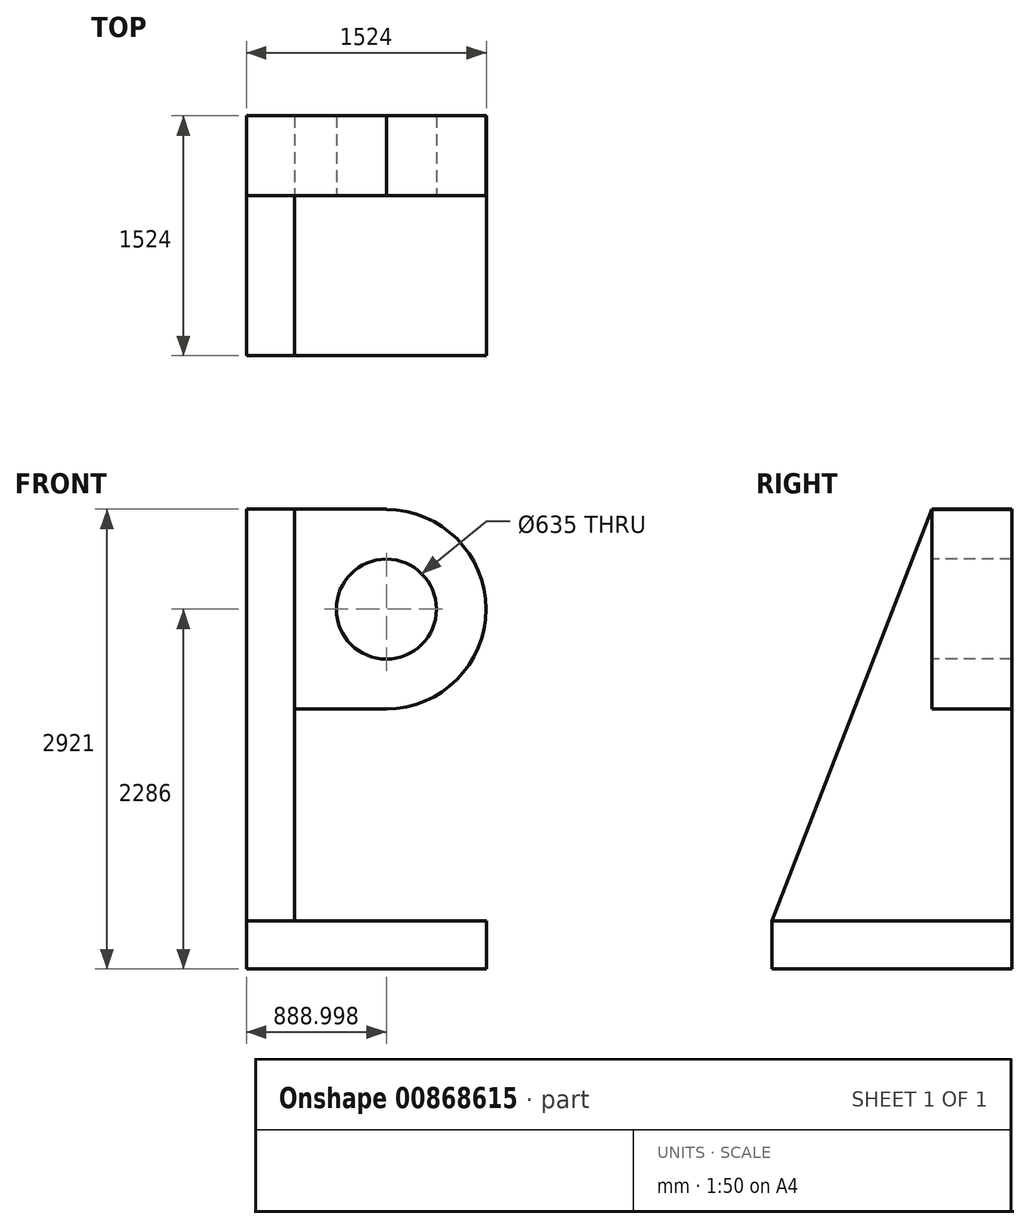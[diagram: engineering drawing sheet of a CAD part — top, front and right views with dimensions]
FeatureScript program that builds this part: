
annotation { "Feature Type Name" : "Feature", "Feature Type Description" : "" }
export const myFeature = defineFeature(function(context is Context, id is Id, definition is map)
    precondition{}
    {
        {
            var Q0;
            Q0=qCreatedBy(makeId("Top.planeOp"),FACE);
            var sketch = newSketch(context, id + "F0", { "sketchPlane" : qUnion([Q0])});
            skLineSegment(sketch, "E0", {"start": v(1363.38, -50.15) * mm, "end": v(-160.62, -50.15) * mm});
            skLineSegment(sketch, "E1", {"start": v(1363.38, -50.15) * mm, "end": v(1363.38, 1473.85) * mm});
            skLineSegment(sketch, "E2", {"start": v(1363.38, 1473.85) * mm, "end": v(-160.62, 1473.85) * mm});
            skLineSegment(sketch, "E3", {"start": v(-160.62, 1473.85) * mm, "end": v(-160.62, -50.15) * mm});
            skSolve(sketch);
        }
        {
            var Q0;
            Q0=makeQuery(id+"F0.imprint","IMPRINT",FACE,{"disambiguationData":[TD([[makeQuery(id+"F0.imprint","IMPRINT",EDGE,{"derivedFrom":sQuery(id+"F0.wireOp",EDGE,"E0")}),-1.0]])]});
            extrude(context, id + "F1", {"entities" : qUnion([Q0]), "depth" : 304.8 * mm, "offsetDistance" : 25.4 * mm});
        }
        {
            var Q0;
            Q0=makeQuery(id+"F1.opExtrude","SWEPT_FACE",FACE,{"disambiguationData":[OSD([sQuery(id+"F0.wireOp",EDGE,"E3")])]});
            var sketch = newSketch(context, id + "F2", { "sketchPlane" : qUnion([Q0])});
            skLineSegment(sketch, "E4", {"start": v(-1473.85, 304.8) * mm, "end": v(-1473.85, 2921) * mm});
            skLineSegment(sketch, "E5", {"start": v(-1473.85, 2921) * mm, "end": v(-965.85, 2921) * mm});
            skLineSegment(sketch, "E6", {"start": v(-965.85, 2921) * mm, "end": v(50.15, 304.8) * mm});
            skSolve(sketch);
        }
        {
            var Q0;
            Q0=makeQuery(id+"F2.imprint","IMPRINT",FACE,{"disambiguationData":[TD([[makeQuery(id+"F2.imprint","IMPRINT",EDGE,{"derivedFrom":sQuery(id+"F2.wireOp",EDGE,"E4")}),-1.0]])]});
            extrude(context, id + "F3", {"entities" : qUnion([Q0]), "operationType" : NewBodyOperationType.ADD, "oppositeDirection" : true, "depth" : 304.8 * mm, "offsetDistance" : 25.4 * mm});
        }
        {
            var Q0;
            Q0=makeQuery(id+"F3.opExtrude","CAP_FACE",FACE,{"disambiguationData":[OSD([sQuery(id+"F0.wireOp",EDGE,"E3"),sQuery(id+"F2.wireOp",EDGE,"E4"),sQuery(id+"F2.wireOp",EDGE,"E5"),sQuery(id+"F2.wireOp",EDGE,"E6")])],"isStart":false});
            var sketch = newSketch(context, id + "F4", { "sketchPlane" : qUnion([Q0])});
            skLineSegment(sketch, "E7", {"start": v(1473.85, 2921) * mm, "end": v(1473.85, 1651) * mm});
            skLineSegment(sketch, "E8", {"start": v(1473.85, 1651) * mm, "end": v(965.85, 1651) * mm});
            skLineSegment(sketch, "E9", {"start": v(1473.85, 2921) * mm, "end": v(965.85, 2921) * mm});
            skLineSegment(sketch, "E10", {"start": v(965.85, 2921) * mm, "end": v(965.85, 1651) * mm});
            skSolve(sketch);
        }
        {
            var Q0;
            Q0=makeQuery(id+"F4.imprint","IMPRINT",FACE,{"disambiguationData":[TD([[makeQuery(id+"F4.imprint","IMPRINT",EDGE,{"derivedFrom":sQuery(id+"F4.wireOp",EDGE,"E7")}),1.0]])]});
            extrude(context, id + "F5", {"entities" : qUnion([Q0]), "operationType" : NewBodyOperationType.ADD, "depth" : 584.2 * mm, "offsetDistance" : 25.4 * mm});
        }
        {
            var Q0;
            Q0=makeQuery(id+"F5.opExtrude","SWEPT_FACE",FACE,{"disambiguationData":[OSD([sQuery(id+"F4.wireOp",EDGE,"E10")])]});
            var sketch = newSketch(context, id + "F6", { "sketchPlane" : qUnion([Q0])});
            skCircle(sketch, "E11", {"center": v(728.38, 2286) * mm, "radius": 633.05 * mm});
            skSolve(sketch);
        }
        {
            var Q0;
            {var subQ0=sQuery(id+"F6.wireOp",EDGE,"E11");var subQ1=makeQuery(id+"F5.opExtrude","CAP_EDGE",EDGE,{"disambiguationData":[OSD([sQuery(id+"F4.wireOp",EDGE,"E10")])],"isStart":false});var subQ2=makeQuery(id+"F6.imprint","INTERSECT",VERTEX,{"disambiguationData":[OD(0.0)],"derivedFrom":[subQ1,subQ0]});Q0=makeQuery(id+"F6.imprint","IMPRINT",FACE,{"disambiguationData":[TD([[makeQuery(id+"F6.imprint","IMPRINT",EDGE,{"disambiguationData":[TD([[subQ2,1.0]])],"derivedFrom":subQ0}),1.0]])]});}
            extrude(context, id + "F7", {"entities" : qUnion([Q0]), "operationType" : NewBodyOperationType.ADD, "oppositeDirection" : true, "depth" : 508 * mm, "offsetDistance" : 25.4 * mm});
        }
        {
            var Q0;
            {var subQ0=sQuery(id+"F4.wireOp",EDGE,"E10");Q0=makeQuery(id+"F7.boolean.opBoolean","MERGE",FACE,{"derivedFrom":[makeQuery(id+"F5.opExtrude","SWEPT_FACE",FACE,{"disambiguationData":[OSD([subQ0])]}),makeQuery(id+"F7.opExtrude","CAP_FACE",FACE,{"disambiguationData":[OSD([subQ0,sQuery(id+"F6.wireOp",EDGE,"E11")])],"isStart":true})]});}
            var sketch = newSketch(context, id + "F8", { "sketchPlane" : qUnion([Q0])});
            skCircle(sketch, "E12", {"center": v(728.38, 2286) * mm, "radius": 317.5 * mm});
            skSolve(sketch);
        }
        {
            var Q0;
            Q0=makeQuery(id+"F8.imprint","IMPRINT",FACE,{"disambiguationData":[TD([[makeQuery(id+"F8.imprint","IMPRINT",EDGE,{"derivedFrom":sQuery(id+"F8.wireOp",EDGE,"E12")}),1.0]])]});
            extrude(context, id + "F9", {"entities" : qUnion([Q0]), "operationType" : NewBodyOperationType.REMOVE, "oppositeDirection" : true, "depth" : 508 * mm, "offsetDistance" : 25.4 * mm});
        }
    });
